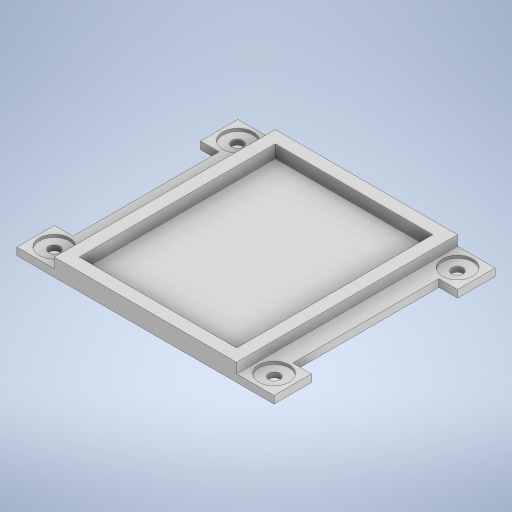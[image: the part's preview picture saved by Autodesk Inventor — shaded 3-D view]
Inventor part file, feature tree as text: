
AUTODESK INVENTOR PART (.ipt)
format: ipt  version: 2023 (Build 270158000, 158)  size: 318,464 bytes
history: native  units: mm
features: extrude x5, sketch x5, other x1
ambient origin geometry x8: Origin, YZ Plane, XZ Plane, XY Plane, X Axis, Y Axis, Z Axis, Center Point
bodies: Body1 (feature_tree)
feature tree (11):
  other  "Sólido1"
  extrude  "Extrusión1"  Depth=5.0mm
  extrude  "Extrusión2"  Depth=78.6mm
  extrude  "Extrusión3"  Depth=7.0mm
  extrude  "Extrusión4"  Depth=15.0mm
  extrude  "Extrusión5"  Depth=15.0mm
  sketch  "Boceto1"  dims[d0=78.6mm d1=63.1mm d2=5.0mm]
  sketch  "Boceto2"  dims[d3=2.0mm d4=0.0mm d5=78.6mm d6=63.1mm d7=5.0mm]
  sketch  "Boceto3"  dims[d8=7.0mm d9=0.0mm d10=12.2mm]
  sketch  "Boceto4"  dims[d11=15.0mm d12=15.0mm]
  sketch  "Boceto5"  dims[d13=3.0mm d14=0.0mm d15=12.2mm d16=15.0mm d17=15.0mm d18=1.0mm d19=0.0mm d20=4.5mm d21=2.0mm d22=0.0mm]
